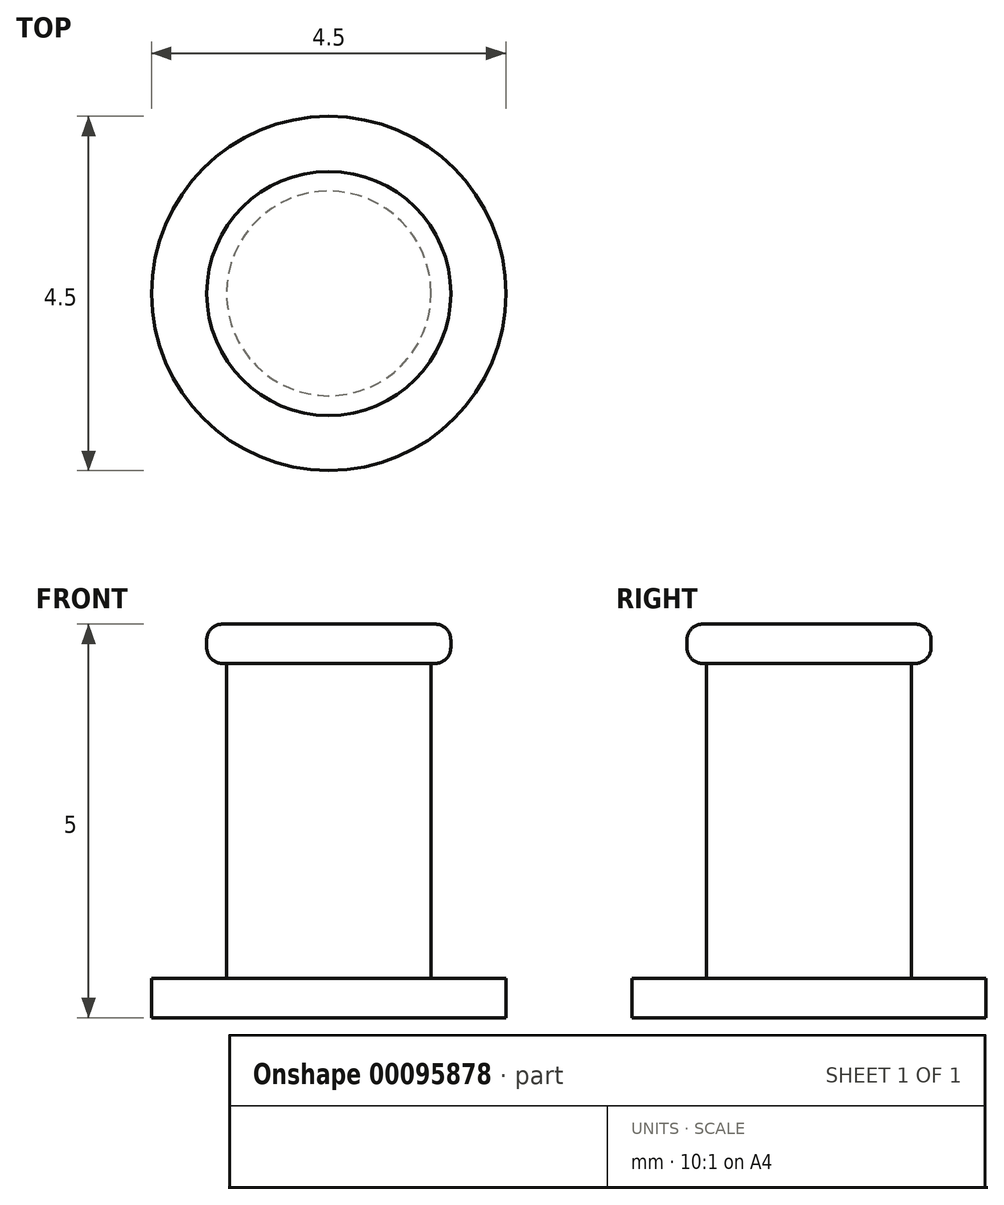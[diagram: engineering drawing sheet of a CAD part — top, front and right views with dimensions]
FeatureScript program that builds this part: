
annotation { "Feature Type Name" : "Feature", "Feature Type Description" : "" }
export const myFeature = defineFeature(function(context is Context, id is Id, definition is map)
    precondition{}
    {
        {
            var Q0;
            Q0=qCreatedBy(makeId("Top.planeOp"),FACE);
            var sketch = newSketch(context, id + "F0", { "sketchPlane" : qUnion([Q0])});
            skCircle(sketch, "E0", {"center": v(0, 0) * mm, "radius": 2.25 * mm});
            skCircle(sketch, "E1", {"center": v(0, 0) * mm, "radius": 1.5 * mm});
            skCircle(sketch, "E2", {"center": v(0, 0) * mm, "radius": 1.3 * mm});
            skSolve(sketch);
        }
        {
            var Q0;
            Q0=makeQuery(id+"F0.imprint","IMPRINT",FACE,{"disambiguationData":[TD([[makeQuery(id+"F0.imprint","IMPRINT",EDGE,{"derivedFrom":sQuery(id+"F0.wireOp",EDGE,"E1")}),1.0]])]});
            var Q1;
            Q1=makeQuery(id+"F0.imprint","IMPRINT",FACE,{"disambiguationData":[TD([[makeQuery(id+"F0.imprint","IMPRINT",EDGE,{"derivedFrom":sQuery(id+"F0.wireOp",EDGE,"E0")}),1.0]])]});
            var Q2;
            Q2=makeQuery(id+"F0.imprint","IMPRINT",FACE,{"disambiguationData":[TD([[makeQuery(id+"F0.imprint","IMPRINT",EDGE,{"derivedFrom":sQuery(id+"F0.wireOp",EDGE,"E2")}),1.0]])]});
            extrude(context, id + "F1", {"entities" : qUnion([Q0, Q1, Q2]), "depth" : 0.5 * mm});
        }
        {
            var Q0;
            Q0=makeQuery(id+"F0.imprint","IMPRINT",FACE,{"disambiguationData":[TD([[makeQuery(id+"F0.imprint","IMPRINT",EDGE,{"derivedFrom":sQuery(id+"F0.wireOp",EDGE,"E2")}),1.0]])]});
            extrude(context, id + "F2", {"entities" : qUnion([Q0]), "operationType" : NewBodyOperationType.ADD, "depth" : 5 * mm});
        }
        {
            var Q0;
            Q0=makeQuery(id+"F2.opExtrude","CAP_FACE",FACE,{"disambiguationData":[OSD([sQuery(id+"F0.wireOp",EDGE,"E2")])],"isStart":false});
            var sketch = newSketch(context, id + "F3", { "sketchPlane" : qUnion([Q0])});
            skCircle(sketch, "E3", {"center": v(0, 0) * mm, "radius": 1.55 * mm});
            skSolve(sketch);
        }
        {
            var Q0;
            Q0 = qSketchRegion(id + "F3", true);
            extrude(context, id + "F4", {"entities" : qUnion([Q0]), "operationType" : NewBodyOperationType.ADD, "oppositeDirection" : true, "depth" : 0.5 * mm});
        }
        {
            var Q0;
            Q0=makeQuery(id+"F4.opExtrude","CAP_EDGE",EDGE,{"disambiguationData":[OSD([sQuery(id+"F3.wireOp",EDGE,"E3")])],"isStart":false});
            var Q1;
            Q1=makeQuery(id+"F4.opExtrude","CAP_EDGE",EDGE,{"disambiguationData":[OSD([sQuery(id+"F3.wireOp",EDGE,"E3")])],"isStart":true});
            fillet(context, id + "F5", {"entities" : qUnion([Q0, Q1]), "radius" : 0.2 * mm, "tangentPropagation" : true, "allowEdgeOverflow" : false});
        }
    });
